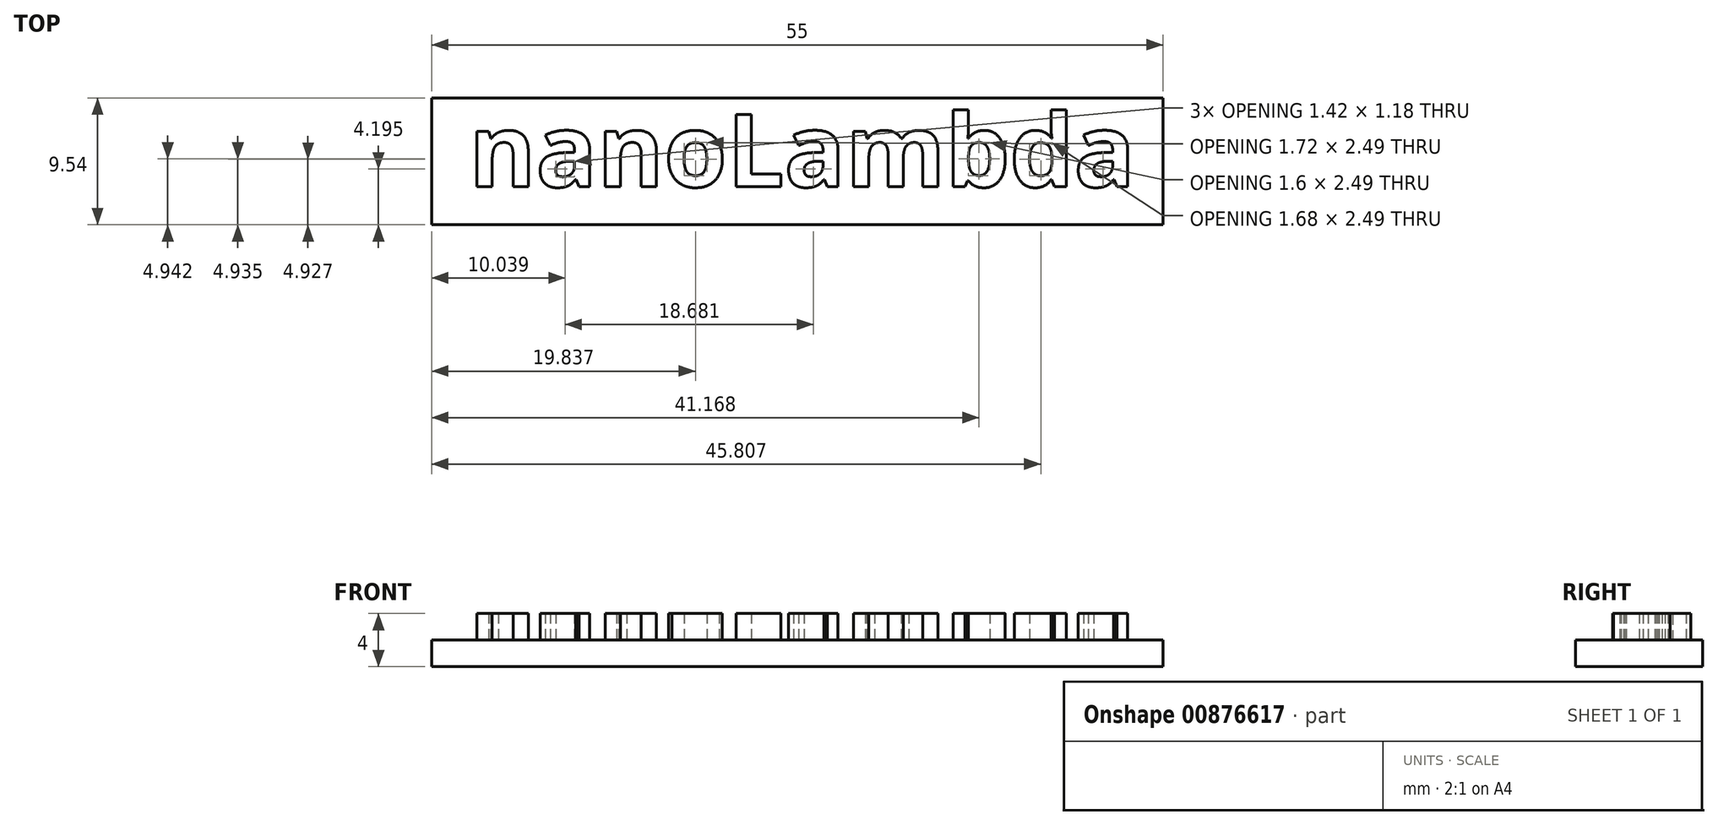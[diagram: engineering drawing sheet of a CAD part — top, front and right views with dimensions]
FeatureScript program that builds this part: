
annotation { "Feature Type Name" : "Feature", "Feature Type Description" : "" }
export const myFeature = defineFeature(function(context is Context, id is Id, definition is map)
    precondition{}
    {
        {
            var Q0;
            Q0=qCreatedBy(makeId("Top.planeOp"),FACE);
            var sketch = newSketch(context, id + "F0", { "sketchPlane" : qUnion([Q0])});
            skText(sketch, "E0", { "text": "nanoLambda", "fontName": "OpenSans-Bold.ttf"});
            const initialGuessF0  = {"E0": [-0.00813, -0.00286, 1, 0, 0.0055]};
            skSetInitialGuess(sketch, initialGuessF0);
            skSolve(sketch);
        }
        {
            var Q0;
            Q0 = qSketchRegion(id + "F0", true);
            extrude(context, id + "F1", {"entities" : qUnion([Q0]), "depth" : 2 * mm, "offsetDistance" : 25 * mm});
        }
        {
            var Q0;
            Q0=qCreatedBy(makeId("Top.planeOp"),FACE);
            var sketch = newSketch(context, id + "F2", { "sketchPlane" : qUnion([Q0])});
            skLineSegment(sketch, "E1.bottom", {"start": v(-10.95, 3.83) * mm, "end": v(44.05, 3.83) * mm});
            skLineSegment(sketch, "E1.top", {"start": v(-10.95, -5.71) * mm, "end": v(44.05, -5.71) * mm});
            skLineSegment(sketch, "E1.left", {"start": v(-10.95, 3.83) * mm, "end": v(-10.95, -5.71) * mm});
            skLineSegment(sketch, "E1.right", {"start": v(44.05, 3.83) * mm, "end": v(44.05, -5.71) * mm});
            skSolve(sketch);
        }
        {
            var Q0;
            Q0 = qSketchRegion(id + "F2", true);
            extrude(context, id + "F3", {"entities" : qUnion([Q0]), "oppositeDirection" : true, "depth" : 2 * mm, "offsetDistance" : 25 * mm});
        }
    });
